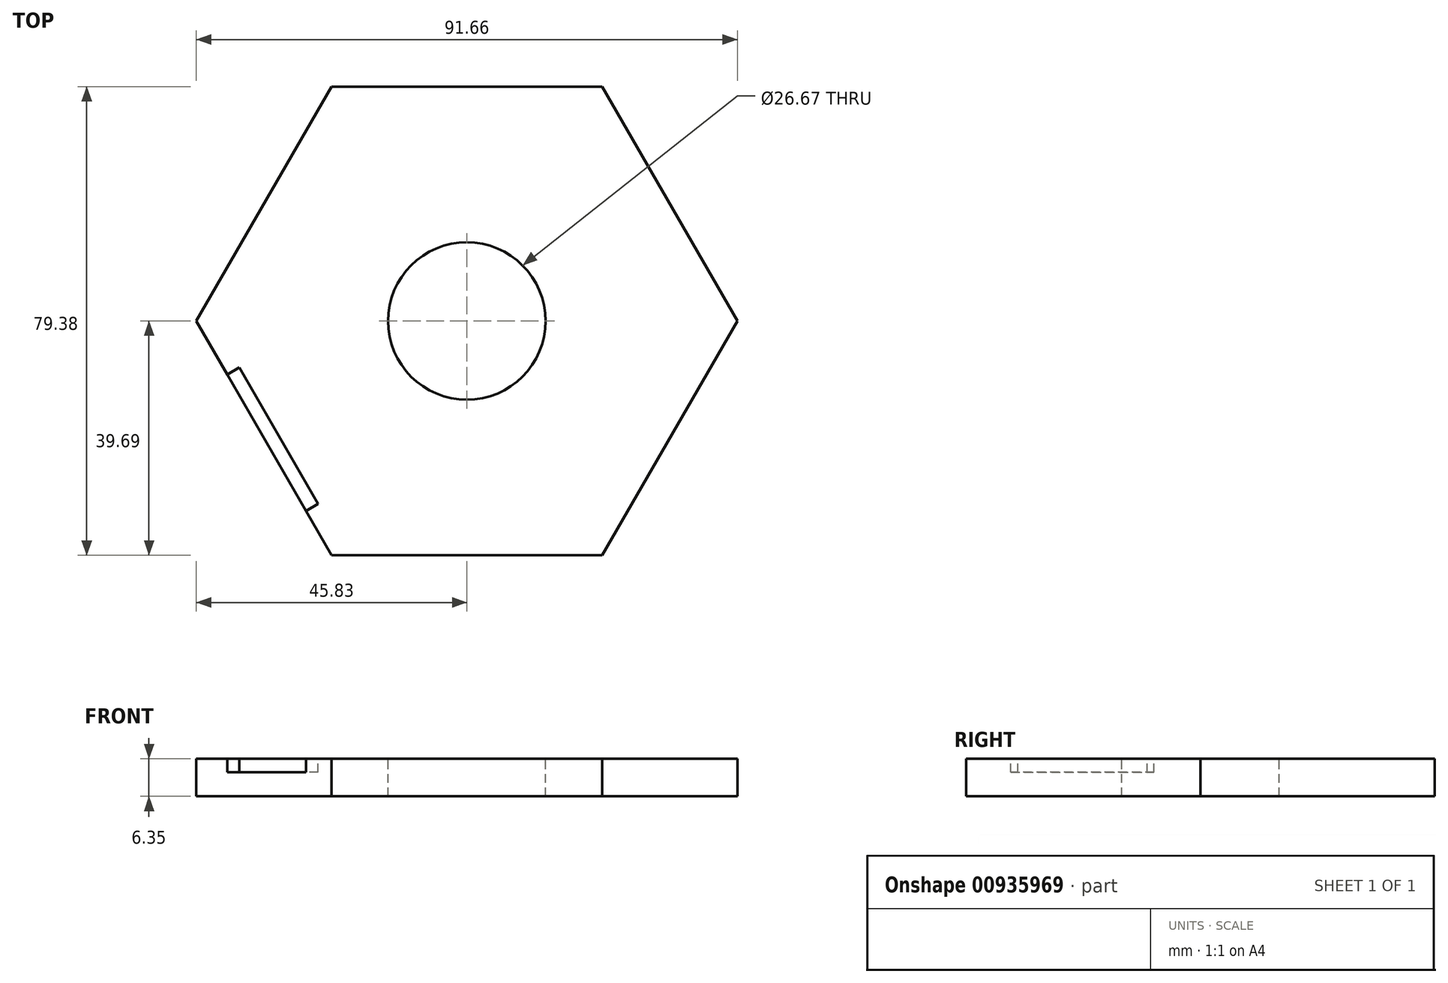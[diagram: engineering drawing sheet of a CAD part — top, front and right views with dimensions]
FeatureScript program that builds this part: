
annotation { "Feature Type Name" : "Feature", "Feature Type Description" : "" }
export const myFeature = defineFeature(function(context is Context, id is Id, definition is map)
    precondition{}
    {
        {
            var Q0;
            Q0=qCreatedBy(makeId("Top.planeOp"),FACE);
            var sketch = newSketch(context, id + "F0", { "sketchPlane" : qUnion([Q0])});
            skCircle(sketch, "E0.cCircle", {"center": v(0, 0) * mm, "radius": 39.69 * mm, "construction": true});
            skLineSegment(sketch, "E0.0", {"start": v(-22.91, 39.69) * mm, "end": v(22.91, 39.69) * mm});
            skLineSegment(sketch, "E0.1", {"start": v(22.91, 39.69) * mm, "end": v(45.83, 0) * mm});
            skLineSegment(sketch, "E0.2", {"start": v(45.83, 0) * mm, "end": v(22.91, -39.69) * mm});
            skLineSegment(sketch, "E0.3", {"start": v(22.91, -39.69) * mm, "end": v(-22.91, -39.69) * mm});
            skLineSegment(sketch, "E0.4", {"start": v(-22.91, -39.69) * mm, "end": v(-45.83, 0) * mm});
            skLineSegment(sketch, "E0.5", {"start": v(-45.83, 0) * mm, "end": v(-22.91, 39.69) * mm});
            skPoint(sketch, "E0.0.midPoint", {"position": v(0, 39.69) * mm});
            skSolve(sketch);
        }
        {
            var Q0;
            Q0=makeQuery(id+"F0.imprint","IMPRINT",FACE,{"disambiguationData":[TD([[makeQuery(id+"F0.imprint","IMPRINT",EDGE,{"derivedFrom":sQuery(id+"F0.wireOp",EDGE,"E0.0")}),-1.0]])]});
            extrude(context, id + "F1", {"entities" : qUnion([Q0]), "depth" : 6.35 * mm, "offsetDistance" : 25.4 * mm});
        }
        {
            var Q0;
            Q0=makeQuery(id+"F1.opExtrude","CAP_FACE",FACE,{"disambiguationData":[OSD([sQuery(id+"F0.wireOp",EDGE,"E0.0"),sQuery(id+"F0.wireOp",EDGE,"E0.1"),sQuery(id+"F0.wireOp",EDGE,"E0.2"),sQuery(id+"F0.wireOp",EDGE,"E0.3"),sQuery(id+"F0.wireOp",EDGE,"E0.4"),sQuery(id+"F0.wireOp",EDGE,"E0.5")])],"isStart":false});
            var sketch = newSketch(context, id + "F2", { "sketchPlane" : qUnion([Q0])});
            skCircle(sketch, "E1", {"center": v(0, 0) * mm, "radius": 13.34 * mm});
            skSolve(sketch);
        }
        {
            var Q0;
            Q0=makeQuery(id+"F2.imprint","IMPRINT",FACE,{"disambiguationData":[TD([[makeQuery(id+"F2.imprint","IMPRINT",EDGE,{"derivedFrom":sQuery(id+"F2.wireOp",EDGE,"E1")}),1.0]])]});
            extrude(context, id + "F3", {"entities" : qUnion([Q0]), "operationType" : NewBodyOperationType.REMOVE, "oppositeDirection" : true, "depth" : 25.4 * mm, "offsetDistance" : 25.4 * mm});
        }
        {
            var Q0;
            Q0=makeQuery(id+"F1.opExtrude","CAP_FACE",FACE,{"disambiguationData":[OSD([sQuery(id+"F0.wireOp",EDGE,"E0.0"),sQuery(id+"F0.wireOp",EDGE,"E0.1"),sQuery(id+"F0.wireOp",EDGE,"E0.2"),sQuery(id+"F0.wireOp",EDGE,"E0.3"),sQuery(id+"F0.wireOp",EDGE,"E0.4"),sQuery(id+"F0.wireOp",EDGE,"E0.5")])],"isStart":false});
            var sketch = newSketch(context, id + "F4", { "sketchPlane" : qUnion([Q0])});
            skLineSegment(sketch, "E2.0", {"start": v(-22.91, -39.69) * mm, "end": v(-45.83, 0) * mm, "construction": true});
            skLineSegment(sketch, "E3", {"start": v(-40.6, -9.07) * mm, "end": v(-38.53, -7.87) * mm});
            skLineSegment(sketch, "E4", {"start": v(-38.53, -7.87) * mm, "end": v(-25.2, -30.97) * mm});
            skLineSegment(sketch, "E5", {"start": v(-25.2, -30.97) * mm, "end": v(-27.26, -32.16) * mm});
            skLineSegment(sketch, "E6", {"start": v(-27.26, -32.16) * mm, "end": v(-40.6, -9.07) * mm});
            skSolve(sketch);
        }
        {
            var Q0;
            Q0=makeQuery(id+"F4.imprint","IMPRINT",FACE,{"disambiguationData":[TD([[makeQuery(id+"F4.imprint","IMPRINT",EDGE,{"derivedFrom":sQuery(id+"F4.wireOp",EDGE,"E3")}),-1.0]])]});
            extrude(context, id + "F5", {"entities" : qUnion([Q0]), "operationType" : NewBodyOperationType.REMOVE, "oppositeDirection" : true, "depth" : 2.3 * mm, "offsetDistance" : 25.4 * mm});
        }
    });
